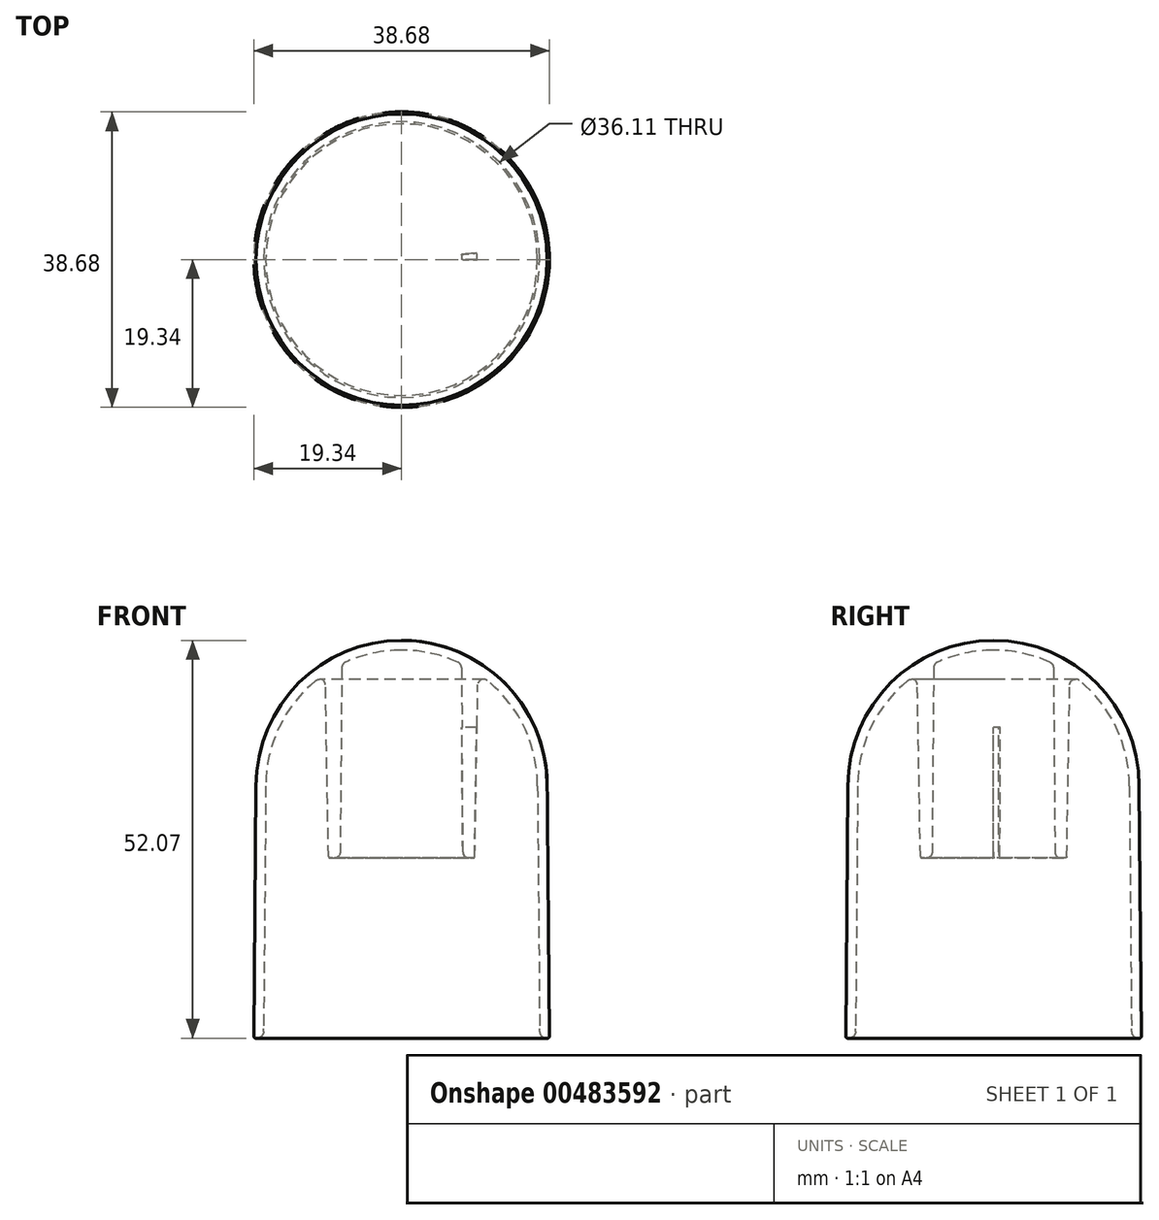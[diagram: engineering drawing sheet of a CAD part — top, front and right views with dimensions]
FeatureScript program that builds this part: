
annotation { "Feature Type Name" : "Feature", "Feature Type Description" : "" }
export const myFeature = defineFeature(function(context is Context, id is Id, definition is map)
    precondition{}
    {
        {
            var Q0;
            Q0=qCreatedBy(makeId("Front.planeOp"),FACE);
            var sketch = newSketch(context, id + "F0", { "sketchPlane" : qUnion([Q0])});
            skLineSegment(sketch, "E0", {"start": v(0, 0) * mm, "end": v(0, 67.4) * mm, "construction": true});
            skLineSegment(sketch, "E1", {"start": v(0, 67.4) * mm, "end": v(0, -87.33) * mm, "construction": true});
            skLineSegment(sketch, "E2", {"start": v(0, 0) * mm, "end": v(-79.27, 0) * mm, "construction": true});
            skLineSegment(sketch, "E3", {"start": v(-79.27, 0) * mm, "end": v(7.97, 0) * mm, "construction": true});
            skPoint(sketch, "E3.endSnap0", {"position": v(-39.63, 0) * mm});
            skArc(sketch, "E4", {"start": v(19.05, 0) * mm, "mid": v(13.47, 13.47) * mm, "end": v(0, 19.05) * mm});
            skLineSegment(sketch, "E5", {"start": v(0, 0) * mm, "end": v(7.97, 0) * mm});
            skLineSegment(sketch, "E6", {"start": v(0, 17.78) * mm, "end": v(0, 19.05) * mm});
            skLineSegment(sketch, "E7", {"start": v(19.05, 0) * mm, "end": v(19.34, -32.76) * mm});
            skLineSegment(sketch, "E8", {"start": v(18.06, -31.75) * mm, "end": v(17.78, 0) * mm});
            skArc(sketch, "E9.0", {"start": v(17.78, 0) * mm, "mid": v(16.05, 7.64) * mm, "end": v(11.21, 13.8) * mm});
            skLineSegment(sketch, "E10.trimOffspring", {"start": v(0, 0) * mm, "end": v(-19.05, 0) * mm});
            skLineSegment(sketch, "E11", {"start": v(19.08, -33.02) * mm, "end": v(18.95, -33.02) * mm});
            skLineSegment(sketch, "E12", {"start": v(18.06, -32.13) * mm, "end": v(18.06, -31.75) * mm});
            skPoint(sketch, "E13.visualSharp", {"position": v(18.06, -33.02) * mm});
            skArc(sketch, "E13.filletArc", {"start": v(18.06, -32.13) * mm, "mid": v(18.32, -32.76) * mm, "end": v(18.95, -33.02) * mm});
            skLineSegment(sketch, "E14", {"start": v(9.4, -9.44) * mm, "end": v(8.8, -9.44) * mm});
            skLineSegment(sketch, "E15", {"start": v(9.58, -9.26) * mm, "end": v(9.97, 13.22) * mm});
            skLineSegment(sketch, "E16", {"start": v(8.04, -8.68) * mm, "end": v(7.83, 15.49) * mm});
            skLineSegment(sketch, "E17.trimOffspring", {"start": v(19.05, 0) * mm, "end": v(121.38, 0) * mm, "construction": true});
            skPoint(sketch, "E18.visualSharp", {"position": v(8.05, -9.44) * mm});
            skArc(sketch, "E18.filletArc", {"start": v(8.04, -8.68) * mm, "mid": v(8.27, -9.22) * mm, "end": v(8.8, -9.44) * mm});
            skArc(sketch, "E19.trimOffspring", {"start": v(7.39, 16.17) * mm, "mid": v(3.78, 17.37) * mm, "end": v(0, 17.78) * mm});
            skPoint(sketch, "E20.visualSharp", {"position": v(10, 14.7) * mm});
            skArc(sketch, "E20.filletArc", {"start": v(11.21, 13.8) * mm, "mid": v(10.4, 13.9) * mm, "end": v(9.97, 13.22) * mm});
            skPoint(sketch, "E21.visualSharp", {"position": v(7.83, 15.96) * mm});
            skArc(sketch, "E21.filletArc", {"start": v(7.83, 15.49) * mm, "mid": v(7.7, 15.9) * mm, "end": v(7.39, 16.17) * mm});
            skPoint(sketch, "E22.visualSharp", {"position": v(19.34, -33.02) * mm});
            skArc(sketch, "E22.filletArc", {"start": v(19.08, -33.02) * mm, "mid": v(19.26, -32.94) * mm, "end": v(19.34, -32.76) * mm});
            skPoint(sketch, "E23.visualSharp", {"position": v(9.57, -9.44) * mm});
            skArc(sketch, "E23.filletArc", {"start": v(9.4, -9.44) * mm, "mid": v(9.52, -9.38) * mm, "end": v(9.58, -9.26) * mm});
            skPoint(sketch, "E24", {"position": v(7.94, 3.4) * mm});
            skLineSegment(sketch, "E25", {"start": v(11.21, 13.8) * mm, "end": v(7.39, 16.17) * mm});
            skSolve(sketch);
        }
        {
            var Q0;
            Q0=makeQuery(id+"F0.imprint","IMPRINT",FACE,{"disambiguationData":[TD([[makeQuery(id+"F0.imprint","IMPRINT",EDGE,{"derivedFrom":sQuery(id+"F0.wireOp",EDGE,"E4")}),1.0]])]});
            var Q1;
            Q1=sQuery(id+"F0.wireOp",EDGE,"E1");
            revolve(context, id + "F1", {"entities" : qUnion([Q0]), "axis" : qUnion([Q1]), "revolveType" : RevolveType.FULL});
        }
        {
            var Q0;
            Q0=makeQuery(id+"F0.imprint","IMPRINT",FACE,{"disambiguationData":[TD([[makeQuery(id+"F0.imprint","IMPRINT",EDGE,{"derivedFrom":sQuery(id+"F0.wireOp",EDGE,"E14")}),-1.0]])]});
            var Q1;
            Q1=sQuery(id+"F0.wireOp",EDGE,"E1");
            revolve(context, id + "F2", {"operationType" : NewBodyOperationType.ADD, "surfaceOperationType" : NewSurfaceOperationType.NEW, "entities" : qUnion([Q0]), "axis" : qUnion([Q1]), "revolveType" : RevolveType.ONE_DIRECTION, "angle" : 360 * degree});
        }
        {
            var Q0;
            Q0=qCreatedBy(makeId("Front.planeOp"),FACE);
            var sketch = newSketch(context, id + "F3", { "sketchPlane" : qUnion([Q0])});
            skLineSegment(sketch, "E26.0", {"start": v(8.04, -8.68) * mm, "end": v(7.9, 7.67) * mm});
            skLineSegment(sketch, "E27.0", {"start": v(9.58, -9.26) * mm, "end": v(9.87, 7.69) * mm});
            skPoint(sketch, "E28.0", {"position": v(9.4, -9.44) * mm});
            skArc(sketch, "E29.0", {"start": v(8.04, -8.68) * mm, "mid": v(8.27, -9.22) * mm, "end": v(8.8, -9.44) * mm});
            skLineSegment(sketch, "E30.1", {"start": v(9.4, -9.44) * mm, "end": v(8.8, -9.44) * mm});
            skPoint(sketch, "E31.0", {"position": v(9.57, -9.44) * mm});
            skArc(sketch, "E32.0", {"start": v(9.4, -9.44) * mm, "mid": v(9.52, -9.38) * mm, "end": v(9.58, -9.26) * mm});
            skLineSegment(sketch, "E33", {"start": v(9.87, 7.69) * mm, "end": v(7.9, 7.67) * mm});
            skPoint(sketch, "E34.orphan", {"position": v(9.97, 13.22) * mm});
            skPoint(sketch, "E35.orphan", {"position": v(7.83, 15.49) * mm});
            skSolve(sketch);
        }
        {
            var Q0;
            Q0=makeQuery(id+"F0Yewx4osn4JRz7_1.2.F3.imprint","IMPRINT",FACE,{"disambiguationData":[TD([[makeQuery(id+"F0Yewx4osn4JRz7_1.2.F3.imprint","IMPRINT",EDGE,{"derivedFrom":sQuery(id+"F0Yewx4osn4JRz7_1.2.F3.wireOp",EDGE,"E26.0")}),-1.0]])]});
            var Q1;
            Q1=makeQuery(id+"F3.imprint","IMPRINT",FACE,{"disambiguationData":[TD([[makeQuery(id+"F3.imprint","IMPRINT",EDGE,{"derivedFrom":sQuery(id+"F3.wireOp",EDGE,"E26.0")}),-1.0]])]});
            var Q2;
            Q2=makeQuery(id+"F0Yewx4osn4JRz7_1.1.F3.imprint","IMPRINT",FACE,{"disambiguationData":[TD([[makeQuery(id+"F0Yewx4osn4JRz7_1.1.F3.imprint","IMPRINT",EDGE,{"derivedFrom":sQuery(id+"F0Yewx4osn4JRz7_1.1.F3.wireOp",EDGE,"E26.0")}),-1.0]])]});
            var Q3;
            Q3=sQuery(id+"F0.wireOp",EDGE,"E1");
            revolve(context, id + "F4", {"operationType" : NewBodyOperationType.REMOVE, "surfaceOperationType" : NewSurfaceOperationType.NEW, "entities" : qUnion([Q0, Q1, Q2]), "axis" : qUnion([Q3]), "revolveType" : RevolveType.ONE_DIRECTION, "oppositeDirection" : true, "angle" : 5 * degree});
        }
    });
